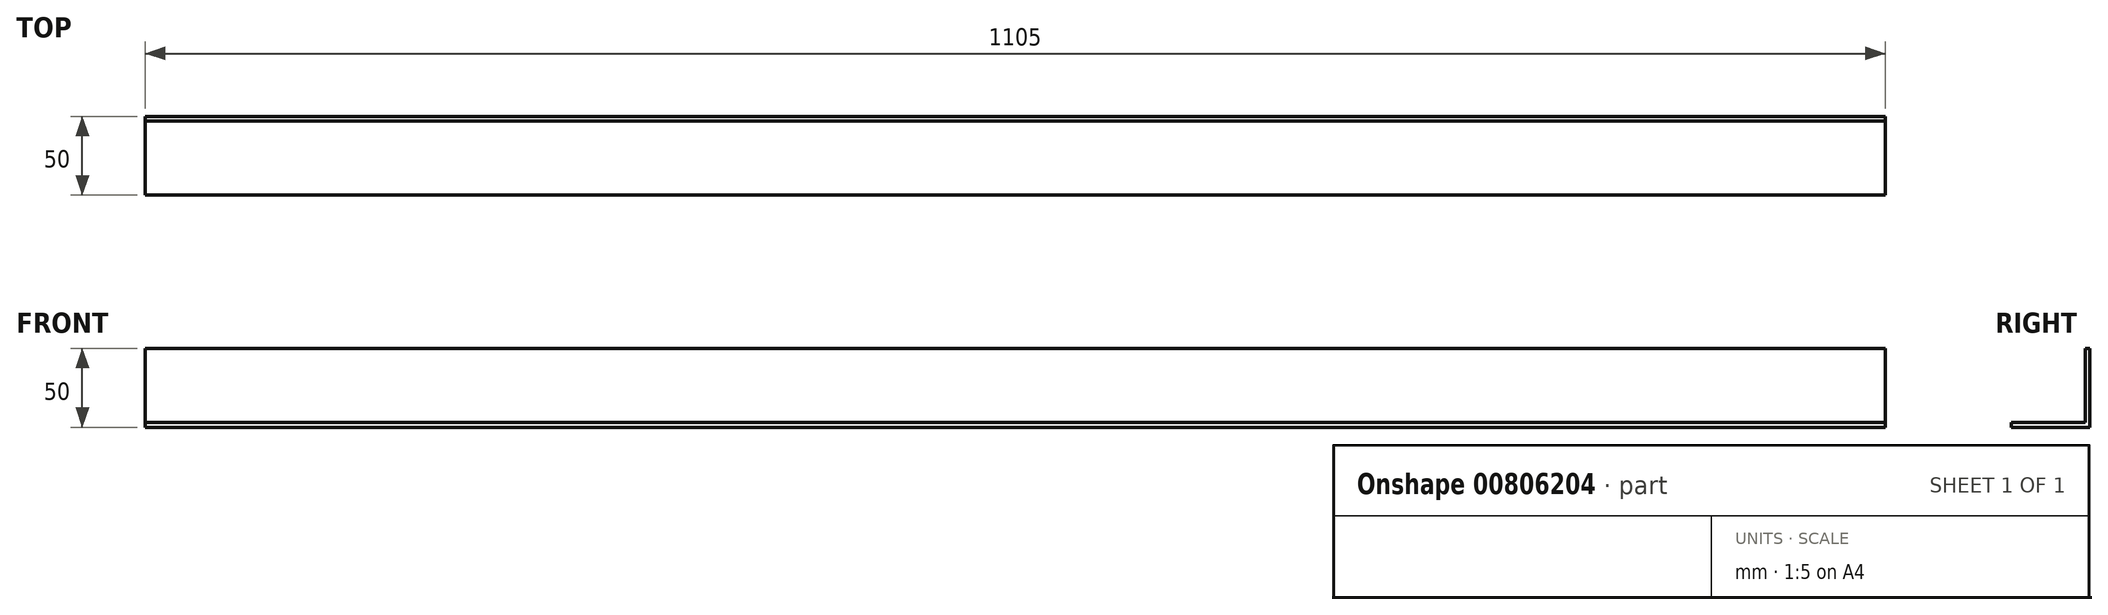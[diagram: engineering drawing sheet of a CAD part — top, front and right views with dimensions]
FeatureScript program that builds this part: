
annotation { "Feature Type Name" : "Feature", "Feature Type Description" : "" }
export const myFeature = defineFeature(function(context is Context, id is Id, definition is map)
    precondition{}
    {
        {
            var Q0;
            Q0=qCreatedBy(makeId("Right.planeOp"),FACE);
            var sketch = newSketch(context, id + "F0", { "sketchPlane" : qUnion([Q0])});
            skLineSegment(sketch, "E0", {"start": v(0, 0) * mm, "end": v(0, 50) * mm});
            skLineSegment(sketch, "E1", {"start": v(0, 0) * mm, "end": v(-50, 0) * mm});
            skLineSegment(sketch, "E2.0", {"start": v(-3, 3) * mm, "end": v(-3, 50) * mm});
            skLineSegment(sketch, "E2.1", {"start": v(-3, 3) * mm, "end": v(-50, 3) * mm});
            skLineSegment(sketch, "E3", {"start": v(0, 50) * mm, "end": v(-3, 50) * mm});
            skLineSegment(sketch, "E4", {"start": v(-50, 0) * mm, "end": v(-50, 3) * mm});
            skSolve(sketch);
        }
        {
            var Q0;
            Q0=qSketchRegion(id+"F0",true);
            extrude(context, id + "F1", {"entities" : qUnion([Q0]), "depth" : 1105 * mm, "offsetDistance" : 25 * mm});
        }
    });
